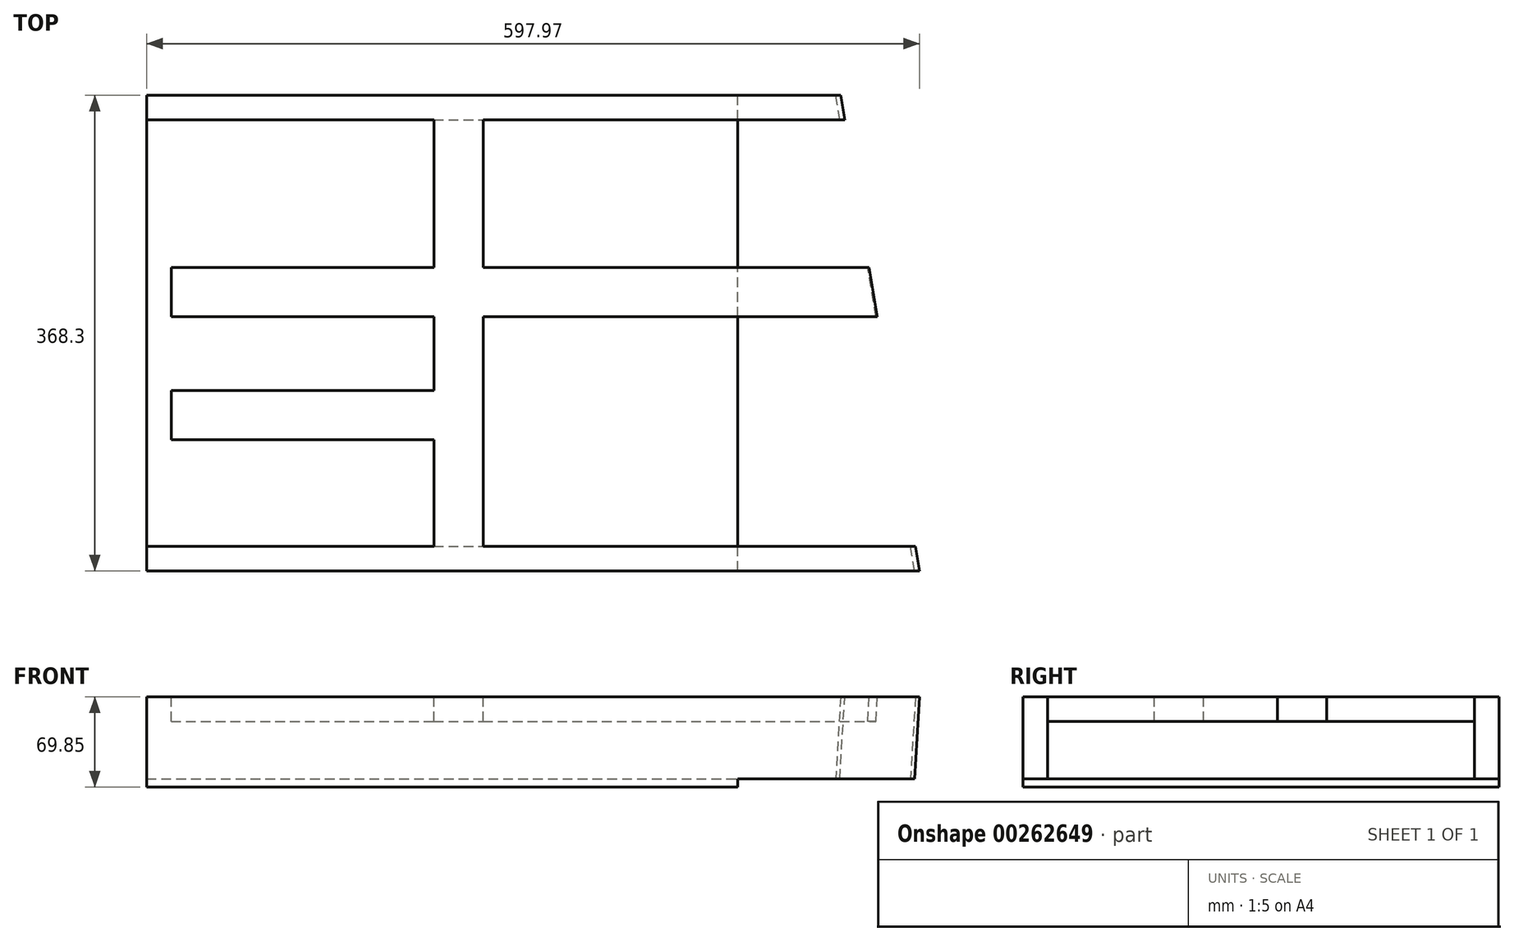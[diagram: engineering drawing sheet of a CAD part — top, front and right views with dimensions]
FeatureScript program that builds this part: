
annotation { "Feature Type Name" : "Feature", "Feature Type Description" : "" }
export const myFeature = defineFeature(function(context is Context, id is Id, definition is map)
    precondition{}
    {
        {
            var Q0;
            Q0=qCreatedBy(makeId("Top.planeOp"),FACE);
            var sketch = newSketch(context, id + "F0", { "sketchPlane" : qUnion([Q0])});
            skLineSegment(sketch, "E0.bottom", {"start": v(0, 0) * mm, "end": v(457.2, 0) * mm});
            skLineSegment(sketch, "E0.top", {"start": v(0, 368.3) * mm, "end": v(457.2, 368.3) * mm});
            skLineSegment(sketch, "E0.left", {"start": v(0, 0) * mm, "end": v(0, 368.3) * mm});
            skLineSegment(sketch, "E0.right", {"start": v(457.2, 0) * mm, "end": v(457.2, 368.3) * mm});
            skSolve(sketch);
        }
        {
            var Q0;
            Q0=makeQuery(id+"F0.imprint","IMPRINT",FACE,{"disambiguationData":[TD([[makeQuery(id+"F0.imprint","IMPRINT",EDGE,{"derivedFrom":sQuery(id+"F0.wireOp",EDGE,"E0.bottom")}),1.0]])]});
            extrude(context, id + "F1", {"entities" : qUnion([Q0]), "depth" : 6.35 * mm, "offsetDistance" : 25.4 * mm});
        }
        {
            var Q0;
            Q0=makeQuery(id+"F1.opExtrude","CAP_FACE",FACE,{"disambiguationData":[OSD([sQuery(id+"F0.wireOp",EDGE,"E0.bottom"),sQuery(id+"F0.wireOp",EDGE,"E0.top"),sQuery(id+"F0.wireOp",EDGE,"E0.left"),sQuery(id+"F0.wireOp",EDGE,"E0.right")])],"isStart":false});
            var sketch = newSketch(context, id + "F2", { "sketchPlane" : qUnion([Q0])});
            skLineSegment(sketch, "E1.bottom", {"start": v(0, 0) * mm, "end": v(635, 0) * mm});
            skLineSegment(sketch, "E1.top", {"start": v(0, 19.05) * mm, "end": v(635, 19.05) * mm});
            skLineSegment(sketch, "E1.left", {"start": v(0, 0) * mm, "end": v(0, 19.05) * mm});
            skLineSegment(sketch, "E2.bottom", {"start": v(457.2, 368.3) * mm, "end": v(0, 368.3) * mm});
            skLineSegment(sketch, "E2.top", {"start": v(635, 349.25) * mm, "end": v(0, 349.25) * mm});
            skLineSegment(sketch, "E2.right", {"start": v(0, 368.3) * mm, "end": v(0, 349.25) * mm});
            skLineSegment(sketch, "E3.bottom", {"start": v(0, 349.25) * mm, "end": v(19.05, 349.25) * mm});
            skLineSegment(sketch, "E3.top", {"start": v(0, 19.05) * mm, "end": v(19.05, 19.05) * mm});
            skLineSegment(sketch, "E3.left", {"start": v(0, 349.25) * mm, "end": v(0, 19.05) * mm});
            skLineSegment(sketch, "E3.right", {"start": v(19.05, 349.25) * mm, "end": v(19.05, 19.05) * mm});
            skLineSegment(sketch, "E4", {"start": v(457.2, 368.3) * mm, "end": v(635, 368.3) * mm});
            skLineSegment(sketch, "E5", {"start": v(635, 484.77) * mm, "end": v(635, -141.66) * mm});
            skSolve(sketch);
        }
        {
            var Q0;
            Q0=makeQuery(id+"F2.imprint","IMPRINT",FACE,{"disambiguationData":[TD([[makeQuery(id+"F2.imprint","IMPRINT",EDGE,{"derivedFrom":sQuery(id+"F2.wireOp",EDGE,"E3.bottom")}),-1.0]])]});
            var Q1;
            Q1=makeQuery(id+"F2.imprint","IMPRINT",FACE,{"disambiguationData":[TD([[makeQuery(id+"F2.imprint","IMPRINT",EDGE,{"derivedFrom":sQuery(id+"F2.wireOp",EDGE,"E2.bottom")}),-1.0]])]});
            var Q2;
            Q2=makeQuery(id+"F2.imprint","IMPRINT",FACE,{"disambiguationData":[TD([[makeQuery(id+"F2.imprint","IMPRINT",EDGE,{"derivedFrom":sQuery(id+"F2.wireOp",EDGE,"E1.bottom")}),1.0]])]});
            var Q3;
            {var subQ0=sQuery(id+"F2.wireOp",EDGE,"E1.left");Q3=makeQuery(id+"F2.imprint","IMPRINT",FACE,{"disambiguationData":[TD([[makeQuery(id+"F2.imprint","IMPRINT",EDGE,{"derivedFrom":subQ0}),-1.0]])]});}
            var Q4;
            {var subQ0=sQuery(id+"F2.wireOp",EDGE,"x07iYHST-ARmc-FDgu-L4I3-qFsh8s1Gas1N");Q4=makeQuery(id+"F2.imprint","IMPRINT",FACE,{"disambiguationData":[TD([[makeQuery(id+"F2.imprint","IMPRINT",EDGE,{"derivedFrom":subQ0}),-1.0]])]});}
            var Q5;
            {var subQ5=sQuery(id+"F2.wireOp",EDGE,"E4");Q5=makeQuery(id+"F2.imprint","IMPRINT",FACE,{"disambiguationData":[TD([[makeQuery(id+"F2.imprint","IMPRINT",EDGE,{"derivedFrom":subQ5}),-1.0]])]});}
            extrude(context, id + "F3", {"entities" : qUnion([Q0, Q1, Q2, Q3, Q4, Q5]), "operationType" : NewBodyOperationType.ADD, "depth" : 63.5 * mm, "offsetDistance" : 25.4 * mm});
        }
        {
            var Q0;
            Q0=makeQuery(id+"F3.opExtrude","CAP_FACE",FACE,{"disambiguationData":[OSD([sQuery(id+"F2.wireOp",EDGE,"E1.bottom"),sQuery(id+"F2.wireOp",EDGE,"E1.top"),sQuery(id+"F2.wireOp",EDGE,"E1.left"),sQuery(id+"F2.wireOp",EDGE,"E1.right"),sQuery(id+"F2.wireOp",EDGE,"E2.bottom"),sQuery(id+"F2.wireOp",EDGE,"E2.top"),sQuery(id+"F2.wireOp",EDGE,"E2.left"),sQuery(id+"F2.wireOp",EDGE,"E2.right"),sQuery(id+"F2.wireOp",EDGE,"E3.left"),sQuery(id+"F2.wireOp",EDGE,"E3.right")])],"isStart":false});
            var sketch = newSketch(context, id + "F4", { "sketchPlane" : qUnion([Q0])});
            skLineSegment(sketch, "E6.bottom", {"start": v(222.25, 19.05) * mm, "end": v(260.35, 19.05) * mm});
            skLineSegment(sketch, "E6.top", {"start": v(222.25, 349.25) * mm, "end": v(260.35, 349.25) * mm});
            skLineSegment(sketch, "E6.left", {"start": v(222.25, 19.05) * mm, "end": v(222.25, 349.25) * mm});
            skLineSegment(sketch, "E6.right", {"start": v(260.35, 19.05) * mm, "end": v(260.35, 349.25) * mm});
            skLineSegment(sketch, "E7.bottom", {"start": v(19.05, 139.7) * mm, "end": v(222.25, 139.7) * mm});
            skLineSegment(sketch, "E7.top", {"start": v(19.05, 101.6) * mm, "end": v(222.25, 101.6) * mm});
            skLineSegment(sketch, "E7.left", {"start": v(19.05, 139.7) * mm, "end": v(19.05, 101.6) * mm});
            skLineSegment(sketch, "E7.right", {"start": v(222.25, 139.7) * mm, "end": v(222.25, 101.6) * mm});
            skLineSegment(sketch, "E8.bottom", {"start": v(19.05, 234.95) * mm, "end": v(222.25, 234.95) * mm});
            skLineSegment(sketch, "E8.top", {"start": v(19.05, 196.85) * mm, "end": v(222.25, 196.85) * mm});
            skLineSegment(sketch, "E8.left", {"start": v(19.05, 234.95) * mm, "end": v(19.05, 196.85) * mm});
            skLineSegment(sketch, "E8.right", {"start": v(222.25, 234.95) * mm, "end": v(222.25, 196.85) * mm});
            skLineSegment(sketch, "E9.bottom", {"start": v(260.35, 234.95) * mm, "end": v(635, 234.95) * mm});
            skLineSegment(sketch, "E9.top", {"start": v(260.35, 196.85) * mm, "end": v(635, 196.85) * mm});
            skLineSegment(sketch, "E9.left", {"start": v(260.35, 234.95) * mm, "end": v(260.35, 196.85) * mm});
            skLineSegment(sketch, "E9.right", {"start": v(635, 234.95) * mm, "end": v(635, 196.85) * mm});
            skSolve(sketch);
        }
        {
            var Q0;
            Q0=makeQuery(id+"F4.imprint","IMPRINT",FACE,{"disambiguationData":[TD([[makeQuery(id+"F4.imprint","IMPRINT",EDGE,{"derivedFrom":sQuery(id+"F4.wireOp",EDGE,"E7.bottom")}),-1.0]])]});
            var Q1;
            {var subQ3=sQuery(id+"F4.wireOp",EDGE,"E6.bottom");Q1=makeQuery(id+"F4.imprint","IMPRINT",FACE,{"disambiguationData":[TD([[makeQuery(id+"F4.imprint","IMPRINT",EDGE,{"derivedFrom":subQ3}),1.0]])]});}
            var Q2;
            Q2=makeQuery(id+"F4.imprint","IMPRINT",FACE,{"disambiguationData":[TD([[makeQuery(id+"F4.imprint","IMPRINT",EDGE,{"derivedFrom":sQuery(id+"F4.wireOp",EDGE,"E8.bottom")}),-1.0]])]});
            var Q3;
            Q3=makeQuery(id+"F4.imprint","IMPRINT",FACE,{"disambiguationData":[TD([[makeQuery(id+"F4.imprint","IMPRINT",EDGE,{"derivedFrom":sQuery(id+"F4.wireOp",EDGE,"E9.bottom")}),-1.0]])]});
            extrude(context, id + "F5", {"entities" : qUnion([Q0, Q1, Q2, Q3]), "operationType" : NewBodyOperationType.ADD, "oppositeDirection" : true, "depth" : 19.05 * mm, "offsetDistance" : 25.4 * mm});
        }
        {
            var Q0;
            Q0=makeQuery(id+"F3.opExtrude","CAP_EDGE",EDGE,{"disambiguationData":[OSD([sQuery(id+"F2.wireOp",EDGE,"E1.bottom")])],"isStart":false});
            cPlane(context, id + "F6", {"entities" : qUnion([Q0]), "cplaneType" : CPlaneType.LINE_ANGLE, "offset" : 25.4 * mm, "angle" : 110 * degree, "oppositeDirection" : true, "width" : 152.4 * mm, "height" : 152.4 * mm});
        }
        {
            var Q0;
            Q0=qCreatedBy(id+"F6.planeOp",FACE);
            var sketch = newSketch(context, id + "F7", { "sketchPlane" : qUnion([Q0])});
            skLineSegment(sketch, "E10", {"start": v(513.74, -453.79) * mm, "end": v(643.61, 282.72) * mm});
            skLineSegment(sketch, "E11", {"start": v(643.61, 282.72) * mm, "end": v(643.61, -453.79) * mm});
            skLineSegment(sketch, "E12", {"start": v(513.74, -453.79) * mm, "end": v(643.61, -453.79) * mm});
            skSolve(sketch);
        }
        {
            var Q0;
            Q0=makeQuery(id+"F7.imprint","IMPRINT",FACE,{"disambiguationData":[TD([[makeQuery(id+"F7.imprint","IMPRINT",EDGE,{"derivedFrom":sQuery(id+"F7.wireOp",EDGE,"E10")}),-1.0]])]});
            extrude(context, id + "F8", {"entities" : qUnion([Q0]), "operationType" : NewBodyOperationType.REMOVE, "endBound" : BoundingType.THROUGH_ALL, "oppositeDirection" : true, "depth" : 25.4 * mm, "offsetDistance" : 25.4 * mm, "hasSecondDirection" : true, "secondDirectionBound" : SecondDirectionBoundingType.THROUGH_ALL, "secondDirectionOppositeDirection" : false, "secondDirectionDepth" : 25.4 * mm});
        }
    });
